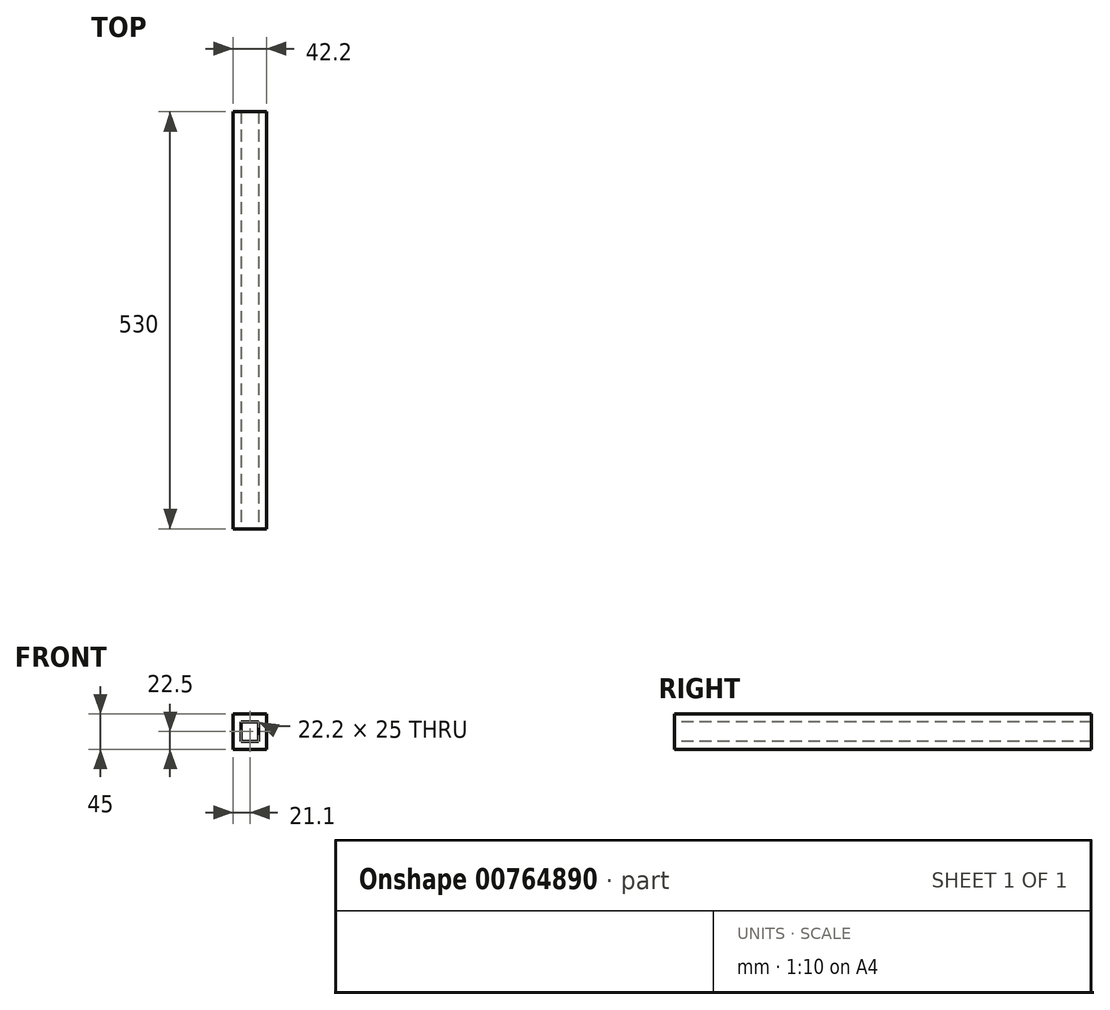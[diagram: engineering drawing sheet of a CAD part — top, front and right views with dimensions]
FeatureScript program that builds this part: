
annotation { "Feature Type Name" : "Feature", "Feature Type Description" : "" }
export const myFeature = defineFeature(function(context is Context, id is Id, definition is map)
    precondition{}
    {
        {
            var Q0;
            Q0=qCreatedBy(makeId("Front.planeOp"),FACE);
            var sketch = newSketch(context, id + "F0", { "sketchPlane" : qUnion([Q0])});
            skLineSegment(sketch, "E0.bottom", {"start": v(0, 0) * mm, "end": v(42.2, 0) * mm});
            skLineSegment(sketch, "E0.top", {"start": v(0, -45) * mm, "end": v(42.2, -45) * mm});
            skLineSegment(sketch, "E0.left", {"start": v(0, 0) * mm, "end": v(0, -45) * mm});
            skLineSegment(sketch, "E0.right", {"start": v(42.2, 0) * mm, "end": v(42.2, -45) * mm});
            skLineSegment(sketch, "E1.0", {"start": v(10, -10) * mm, "end": v(32.2, -10) * mm});
            skLineSegment(sketch, "E2.0", {"start": v(10, -35) * mm, "end": v(32.2, -35) * mm});
            skLineSegment(sketch, "E3.0", {"start": v(32.2, -10) * mm, "end": v(32.2, -35) * mm});
            skLineSegment(sketch, "E4.0", {"start": v(10, -10) * mm, "end": v(10, -35) * mm});
            skSolve(sketch);
        }
        {
            var Q0;
            Q0 = qSketchRegion(id + "F0", true);
            extrude(context, id + "F1", {"entities" : qUnion([Q0]), "oppositeDirection" : true, "depth" : 530 * mm, "offsetDistance" : 25 * mm});
        }
    });
